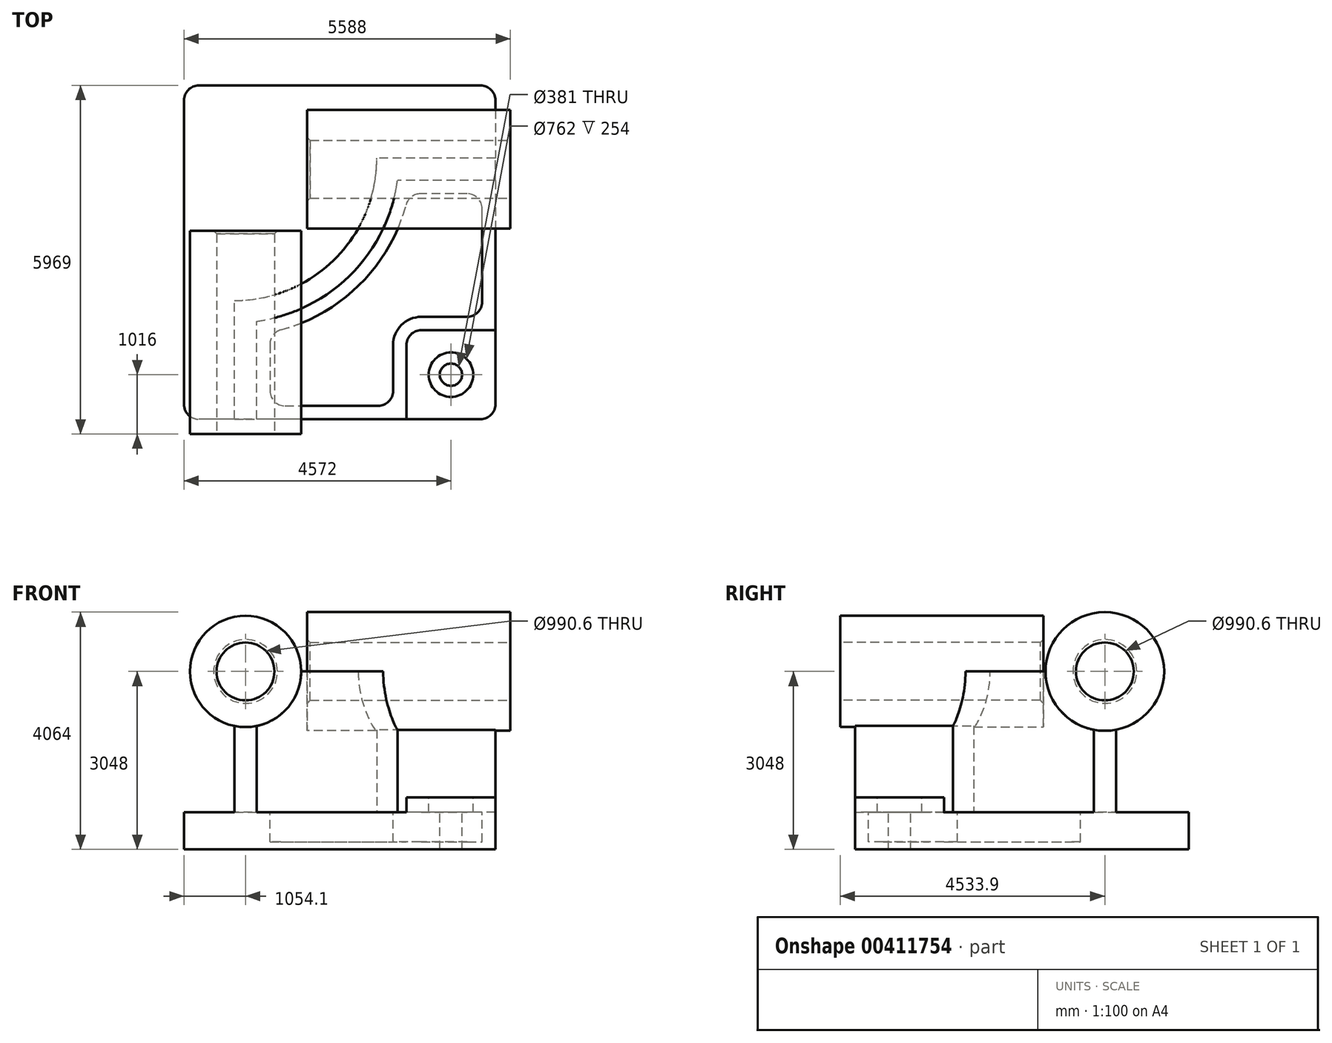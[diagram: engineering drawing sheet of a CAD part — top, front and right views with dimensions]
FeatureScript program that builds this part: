
annotation { "Feature Type Name" : "Feature", "Feature Type Description" : "" }
export const myFeature = defineFeature(function(context is Context, id is Id, definition is map)
    precondition{}
    {
        {
            var Q0;
            Q0=qCreatedBy(makeId("Top.planeOp"),FACE);
            var sketch = newSketch(context, id + "F0", { "sketchPlane" : qUnion([Q0])});
            skLineSegment(sketch, "E0.bottom", {"start": v(2667, 2857.5) * mm, "end": v(-2667, 2857.5) * mm});
            skLineSegment(sketch, "E0.top", {"start": v(2667, -2857.5) * mm, "end": v(-2667, -2857.5) * mm});
            skLineSegment(sketch, "E0.left", {"start": v(2667, 2857.5) * mm, "end": v(2667, -2857.5) * mm});
            skLineSegment(sketch, "E0.right", {"start": v(-2667, 2857.5) * mm, "end": v(-2667, -2857.5) * mm});
            skPoint(sketch, "E0.middle", {"position": v(0, 0) * mm});
            skSolve(sketch);
        }
        {
            var Q0;
            Q0=makeQuery(id+"F0.imprint","IMPRINT",FACE,{"disambiguationData":[TD([[makeQuery(id+"F0.imprint","IMPRINT",EDGE,{"derivedFrom":sQuery(id+"F0.wireOp",EDGE,"E0.bottom")}),1.0]])]});
            extrude(context, id + "F1", {"entities" : qUnion([Q0]), "depth" : 635 * mm});
        }
        {
            var Q0;
            Q0=makeQuery(id+"F1.opExtrude","CAP_FACE",FACE,{"disambiguationData":[OSD([sQuery(id+"F0.wireOp",EDGE,"E0.bottom"),sQuery(id+"F0.wireOp",EDGE,"E0.top"),sQuery(id+"F0.wireOp",EDGE,"E0.left"),sQuery(id+"F0.wireOp",EDGE,"E0.right")])],"isStart":false});
            var sketch = newSketch(context, id + "F2", { "sketchPlane" : qUnion([Q0])});
            skLineSegment(sketch, "E1", {"start": v(-1803.4, -2857.5) * mm, "end": v(-1803.4, -825.5) * mm});
            skLineSegment(sketch, "E2", {"start": v(2667, 1612.9) * mm, "end": v(635, 1612.9) * mm});
            skArc(sketch, "E3", {"start": v(-1803.4, -825.5) * mm, "mid": v(-79.2, -111.3) * mm, "end": v(635, 1612.9) * mm});
            skLineSegment(sketch, "E4", {"start": v(635, 1612.9) * mm, "end": v(-1803.4, 1612.9) * mm, "construction": true});
            skLineSegment(sketch, "E5", {"start": v(-1803.4, 1612.9) * mm, "end": v(-1803.4, -825.5) * mm, "construction": true});
            skLineSegment(sketch, "E6.0", {"start": v(-1422.4, -2857.5) * mm, "end": v(-1422.4, -1180.64) * mm});
            skArc(sketch, "E6.1", {"start": v(-1422.4, -1180.64) * mm, "mid": v(190.22, -380.72) * mm, "end": v(990.14, 1231.9) * mm});
            skLineSegment(sketch, "E6.2", {"start": v(2667, 1231.9) * mm, "end": v(990.14, 1231.9) * mm});
            skLineSegment(sketch, "E7.0", {"start": v(2667, 2857.5) * mm, "end": v(2667, -2857.5) * mm});
            skLineSegment(sketch, "E8.0", {"start": v(2667, -2857.5) * mm, "end": v(-2667, -2857.5) * mm});
            skSolve(sketch);
        }
        {
            var Q0;
            {var subQ2=sQuery(id+"F2.wireOp",EDGE,"E1");Q0=makeQuery(id+"F2.imprint","IMPRINT",FACE,{"disambiguationData":[TD([[makeQuery(id+"F2.imprint","IMPRINT",EDGE,{"derivedFrom":subQ2}),-1.0]])]});}
            extrude(context, id + "F3", {"entities" : qUnion([Q0]), "operationType" : NewBodyOperationType.ADD, "depth" : 2413 * mm});
        }
        {
            var Q0;
            Q0=makeQuery(id+"F3.boolean.opBoolean","MERGE",FACE,{"derivedFrom":[makeQuery(id+"F1.opExtrude","SWEPT_FACE",FACE,{"disambiguationData":[OSD([sQuery(id+"F0.wireOp",EDGE,"E0.top")])]}),makeQuery(id+"F3.opExtrude","SWEPT_FACE",FACE,{"disambiguationData":[OSD([sQuery(id+"F2.wireOp",EDGE,"E8.0")])]})]});
            var sketch = newSketch(context, id + "F4", { "sketchPlane" : qUnion([Q0])});
            skCircle(sketch, "E9", {"center": v(-1612.9, 3048) * mm, "radius": 952.5 * mm});
            skSolve(sketch);
        }
        {
            var Q0;
            Q0 = qSketchRegion(id + "F4", true);
            extrude(context, id + "F5", {"entities" : qUnion([Q0]), "operationType" : NewBodyOperationType.ADD, "depth" : 254 * mm, "hasSecondDirection" : true, "secondDirectionOppositeDirection" : true, "secondDirectionDepth" : 3225.8 * mm});
        }
        {
            var Q0;
            Q0=makeQuery(id+"F3.boolean.opBoolean","MERGE",FACE,{"derivedFrom":[makeQuery(id+"F1.opExtrude","SWEPT_FACE",FACE,{"disambiguationData":[OSD([sQuery(id+"F0.wireOp",EDGE,"E0.left")])]}),makeQuery(id+"F3.opExtrude","SWEPT_FACE",FACE,{"disambiguationData":[OSD([sQuery(id+"F2.wireOp",EDGE,"E7.0")])]})]});
            var sketch = newSketch(context, id + "F6", { "sketchPlane" : qUnion([Q0])});
            skCircle(sketch, "E10", {"center": v(1422.4, 3048) * mm, "radius": 1016 * mm});
            skSolve(sketch);
        }
        {
            var Q0;
            Q0 = qSketchRegion(id + "F6", true);
            extrude(context, id + "F7", {"entities" : qUnion([Q0]), "operationType" : NewBodyOperationType.ADD, "depth" : 254 * mm, "hasSecondDirection" : true, "secondDirectionOppositeDirection" : true, "secondDirectionDepth" : 3225.8 * mm});
        }
        {
            var Q0;
            {var subQ0=sQuery(id+"F0.wireOp",EDGE,"E0.left");var subQ1=sQuery(id+"F0.wireOp",EDGE,"E0.top");Q0=makeQuery(id+"F3.boolean.opBoolean","SPLIT",FACE,{"disambiguationData":[TD([makeQuery(id+"F3.opExtrude","SWEPT_FACE",FACE,{"disambiguationData":[OSD([sQuery(id+"F2.wireOp",EDGE,"E6.0")])]})])],"derivedFrom":makeQuery(id+"F1.opExtrude","CAP_FACE",FACE,{"disambiguationData":[OSD([sQuery(id+"F0.wireOp",EDGE,"E0.bottom"),subQ1,subQ0,sQuery(id+"F0.wireOp",EDGE,"E0.right")])],"isStart":false})});}
            var sketch = newSketch(context, id + "F8", { "sketchPlane" : qUnion([Q0])});
            skLineSegment(sketch, "E11.bottom", {"start": v(2667, -2857.5) * mm, "end": v(1143, -2857.5) * mm});
            skLineSegment(sketch, "E11.top", {"start": v(2667, -1333.5) * mm, "end": v(1143, -1333.5) * mm});
            skLineSegment(sketch, "E11.left", {"start": v(2667, -2857.5) * mm, "end": v(2667, -1333.5) * mm});
            skLineSegment(sketch, "E11.right", {"start": v(1143, -2857.5) * mm, "end": v(1143, -1333.5) * mm});
            skSolve(sketch);
        }
        {
            var Q0;
            Q0 = qSketchRegion(id + "F8", true);
            extrude(context, id + "F9", {"entities" : qUnion([Q0]), "operationType" : NewBodyOperationType.ADD, "depth" : 254 * mm});
        }
        {
            var Q0;
            Q0=makeQuery(id+"F9.opExtrude","SWEPT_EDGE",EDGE,{"disambiguationData":[OSD([sQuery(id+"F8.wireOp",EDGE,"E11.top"),sQuery(id+"F8.wireOp",EDGE,"E11.right")])]});
            fillet(context, id + "F10", {"entities" : qUnion([Q0]), "radius" : 254 * mm, "tangentPropagation" : true, "allowEdgeOverflow" : false});
        }
        {
            var Q0;
            {var subQ0=sQuery(id+"F0.wireOp",EDGE,"E0.left");var subQ1=sQuery(id+"F0.wireOp",EDGE,"E0.top");Q0=makeQuery(id+"F3.boolean.opBoolean","SPLIT",FACE,{"disambiguationData":[TD([makeQuery(id+"F3.opExtrude","SWEPT_FACE",FACE,{"disambiguationData":[OSD([sQuery(id+"F2.wireOp",EDGE,"E6.0")])]})])],"derivedFrom":makeQuery(id+"F1.opExtrude","CAP_FACE",FACE,{"disambiguationData":[OSD([sQuery(id+"F0.wireOp",EDGE,"E0.bottom"),subQ1,subQ0,sQuery(id+"F0.wireOp",EDGE,"E0.right")])],"isStart":false})});}
            var sketch = newSketch(context, id + "F11", { "sketchPlane" : qUnion([Q0])});
            skLineSegment(sketch, "E12.0", {"start": v(-1193.8, -1373.52) * mm, "end": v(-1193.8, -2628.9) * mm});
            skArc(sketch, "E12.1", {"start": v(1183.02, 1003.3) * mm, "mid": v(351.86, -542.36) * mm, "end": v(-1193.8, -1373.52) * mm});
            skLineSegment(sketch, "E12.2", {"start": v(-1193.8, -2628.9) * mm, "end": v(914.4, -2628.9) * mm});
            skLineSegment(sketch, "E12.3", {"start": v(2438.4, 1003.3) * mm, "end": v(1183.02, 1003.3) * mm});
            skLineSegment(sketch, "E12.4", {"start": v(914.4, -2628.9) * mm, "end": v(914.4, -1587.5) * mm});
            skArc(sketch, "E12.5", {"start": v(914.4, -1587.5) * mm, "mid": v(1055.75, -1246.25) * mm, "end": v(1397, -1104.9) * mm});
            skLineSegment(sketch, "E12.6", {"start": v(1397, -1104.9) * mm, "end": v(2438.4, -1104.9) * mm});
            skLineSegment(sketch, "E12.7", {"start": v(2438.4, -1104.9) * mm, "end": v(2438.4, 1003.3) * mm});
            skSolve(sketch);
        }
        {
            var Q0;
            Q0=makeQuery(id+"F11.imprint","IMPRINT",FACE,{"disambiguationData":[TD([[makeQuery(id+"F11.imprint","IMPRINT",EDGE,{"derivedFrom":sQuery(id+"F11.wireOp",EDGE,"E12.0")}),1.0]])]});
            extrude(context, id + "F12", {"entities" : qUnion([Q0]), "operationType" : NewBodyOperationType.REMOVE, "oppositeDirection" : true, "depth" : 508 * mm});
        }
        {
            var Q0;
            Q0=makeQuery(id+"F9.opExtrude","CAP_FACE",FACE,{"disambiguationData":[OSD([sQuery(id+"F8.wireOp",EDGE,"E11.bottom"),sQuery(id+"F8.wireOp",EDGE,"E11.top"),sQuery(id+"F8.wireOp",EDGE,"E11.left"),sQuery(id+"F8.wireOp",EDGE,"E11.right")])],"isStart":false});
            var sketch = newSketch(context, id + "F13", { "sketchPlane" : qUnion([Q0])});
            skCircle(sketch, "E13", {"center": v(1905, -2095.5) * mm, "radius": 381 * mm});
            skSolve(sketch);
        }
        {
            var Q0;
            Q0=sQuery(id+"F13.wireOp",VERTEX,"E13.center");
            var Q1;
            Q1=makeQuery(id+"F1.opExtrude","SWEPT_BODY",BODY,{"disambiguationData":[OSD([sQuery(id+"F0.wireOp",EDGE,"E0.bottom"),sQuery(id+"F0.wireOp",EDGE,"E0.top"),sQuery(id+"F0.wireOp",EDGE,"E0.left"),sQuery(id+"F0.wireOp",EDGE,"E0.right")])]});
            hole(context, id + "F14", {"style" : HoleStyle.C_BORE, "endStyle" : HoleEndStyle.THROUGH, "holeDiameter" : 381 * mm, "cBoreDiameter" : 762 * mm, "cBoreDepth" : 254 * mm, "isTappedThrough" : true, "tappedDepth" : 12.7 * mm, "tapClearance" : 3, "locations" : qUnion([Q0]), "scope" : qUnion([Q1])});
        }
        {
            var Q0;
            Q0=makeQuery(id+"F12.boolean.opBoolean","COPY",EDGE,{"derivedFrom":makeQuery(id+"F12.opExtrude","SWEPT_EDGE",EDGE,{"disambiguationData":[OSD([sQuery(id+"F11.wireOp",EDGE,"E12.0"),sQuery(id+"F11.wireOp",EDGE,"E12.1")])]})});
            var Q1;
            Q1=makeQuery(id+"F12.boolean.opBoolean","COPY",EDGE,{"derivedFrom":makeQuery(id+"F12.opExtrude","SWEPT_EDGE",EDGE,{"disambiguationData":[OSD([sQuery(id+"F11.wireOp",EDGE,"E12.1"),sQuery(id+"F11.wireOp",EDGE,"E12.3")])]})});
            var Q2;
            Q2=makeQuery(id+"F12.boolean.opBoolean","COPY",EDGE,{"derivedFrom":makeQuery(id+"F12.opExtrude","SWEPT_EDGE",EDGE,{"disambiguationData":[OSD([sQuery(id+"F11.wireOp",EDGE,"E12.3"),sQuery(id+"F11.wireOp",EDGE,"E12.7")])]})});
            var Q3;
            Q3=makeQuery(id+"F12.boolean.opBoolean","COPY",EDGE,{"derivedFrom":makeQuery(id+"F12.opExtrude","SWEPT_EDGE",EDGE,{"disambiguationData":[OSD([sQuery(id+"F11.wireOp",EDGE,"E12.6"),sQuery(id+"F11.wireOp",EDGE,"E12.7")])]})});
            var Q4;
            Q4=makeQuery(id+"F12.boolean.opBoolean","COPY",EDGE,{"derivedFrom":makeQuery(id+"F12.opExtrude","SWEPT_EDGE",EDGE,{"disambiguationData":[OSD([sQuery(id+"F11.wireOp",EDGE,"E12.2"),sQuery(id+"F11.wireOp",EDGE,"E12.4")])]})});
            var Q5;
            Q5=makeQuery(id+"F12.boolean.opBoolean","COPY",EDGE,{"derivedFrom":makeQuery(id+"F12.opExtrude","SWEPT_EDGE",EDGE,{"disambiguationData":[OSD([sQuery(id+"F11.wireOp",EDGE,"E12.0"),sQuery(id+"F11.wireOp",EDGE,"E12.2")])]})});
            fillet(context, id + "F15", {"entities" : qUnion([Q0, Q1, Q2, Q3, Q4, Q5]), "radius" : 254 * mm, "tangentPropagation" : true, "allowEdgeOverflow" : false});
        }
        {
            var Q0;
            Q0=makeQuery(id+"F5.opExtrude","CAP_FACE",FACE,{"disambiguationData":[OSD([sQuery(id+"F4.wireOp",EDGE,"E9")])],"isStart":false});
            var sketch = newSketch(context, id + "F16", { "sketchPlane" : qUnion([Q0])});
            skCircle(sketch, "E14", {"center": v(-1612.9, 3048) * mm, "radius": 495.3 * mm});
            skSolve(sketch);
        }
        {
            var Q0;
            Q0 = qSketchRegion(id + "F16", true);
            extrude(context, id + "F17", {"entities" : qUnion([Q0]), "operationType" : NewBodyOperationType.REMOVE, "endBound" : BoundingType.THROUGH_ALL, "oppositeDirection" : true, "depth" : 25.4 * mm});
        }
        {
            var Q0;
            Q0=makeQuery(id+"F7.opExtrude","CAP_FACE",FACE,{"disambiguationData":[OSD([sQuery(id+"F6.wireOp",EDGE,"E10")])],"isStart":false});
            var sketch = newSketch(context, id + "F18", { "sketchPlane" : qUnion([Q0])});
            skCircle(sketch, "E15", {"center": v(1422.4, 3048) * mm, "radius": 495.3 * mm});
            skSolve(sketch);
        }
        {
            var Q0;
            Q0 = qSketchRegion(id + "F18", true);
            extrude(context, id + "F19", {"entities" : qUnion([Q0]), "operationType" : NewBodyOperationType.REMOVE, "endBound" : BoundingType.THROUGH_ALL, "oppositeDirection" : true, "depth" : 25.4 * mm});
        }
        {
            var Q0;
            Q0=makeQuery(id+"F17.boolean.opBoolean","COPY",EDGE,{"derivedFrom":makeQuery(id+"F17.opExtrude","CAP_EDGE",EDGE,{"disambiguationData":[OSD([sQuery(id+"F16.wireOp",EDGE,"E14")])],"isStart":true})});
            var Q1;
            Q1=makeQuery(id+"F19.boolean.opBoolean","COPY",EDGE,{"derivedFrom":makeQuery(id+"F19.opExtrude","CAP_EDGE",EDGE,{"disambiguationData":[OSD([sQuery(id+"F18.wireOp",EDGE,"E15")])],"isStart":true})});
            var Q2;
            Q2=makeQuery(id+"F17.boolean.opBoolean","INTERSECT",EDGE,{"derivedFrom":[makeQuery(id+"F5.opExtrude","CAP_FACE",FACE,{"disambiguationData":[OSD([sQuery(id+"F4.wireOp",EDGE,"E9")])],"isStart":true}),makeQuery(id+"F17.opExtrude","SWEPT_FACE",FACE,{"disambiguationData":[OSD([sQuery(id+"F16.wireOp",EDGE,"E14")])]})]});
            var Q3;
            Q3=makeQuery(id+"F19.boolean.opBoolean","INTERSECT",EDGE,{"derivedFrom":[makeQuery(id+"F7.opExtrude","CAP_FACE",FACE,{"disambiguationData":[OSD([sQuery(id+"F6.wireOp",EDGE,"E10")])],"isStart":true}),makeQuery(id+"F19.opExtrude","SWEPT_FACE",FACE,{"disambiguationData":[OSD([sQuery(id+"F18.wireOp",EDGE,"E15")])]})]});
            chamfer(context, id + "F20", {"entities" : qUnion([Q0, Q1, Q2, Q3]), "width" : 50.8 * mm, "tangentPropagation" : true});
        }
        {
            var Q0;
            Q0=makeQuery(id+"F9.boolean.opBoolean","MERGE",EDGE,{"derivedFrom":[makeQuery(id+"F1.opExtrude","SWEPT_EDGE",EDGE,{"disambiguationData":[OSD([sQuery(id+"F0.wireOp",EDGE,"E0.top"),sQuery(id+"F0.wireOp",EDGE,"E0.left")])]}),makeQuery(id+"F9.opExtrude","SWEPT_EDGE",EDGE,{"disambiguationData":[OSD([sQuery(id+"F8.wireOp",EDGE,"E11.bottom"),sQuery(id+"F8.wireOp",EDGE,"E11.left")])]})]});
            var Q1;
            Q1=makeQuery(id+"F1.opExtrude","SWEPT_EDGE",EDGE,{"disambiguationData":[OSD([sQuery(id+"F0.wireOp",EDGE,"E0.top"),sQuery(id+"F0.wireOp",EDGE,"E0.right")])]});
            var Q2;
            Q2=makeQuery(id+"F1.opExtrude","SWEPT_EDGE",EDGE,{"disambiguationData":[OSD([sQuery(id+"F0.wireOp",EDGE,"E0.bottom"),sQuery(id+"F0.wireOp",EDGE,"E0.left")])]});
            var Q3;
            Q3=makeQuery(id+"F1.opExtrude","SWEPT_EDGE",EDGE,{"disambiguationData":[OSD([sQuery(id+"F0.wireOp",EDGE,"E0.bottom"),sQuery(id+"F0.wireOp",EDGE,"E0.right")])]});
            fillet(context, id + "F21", {"entities" : qUnion([Q0, Q1, Q2, Q3]), "radius" : 254 * mm, "tangentPropagation" : true, "allowEdgeOverflow" : false});
        }
    });
